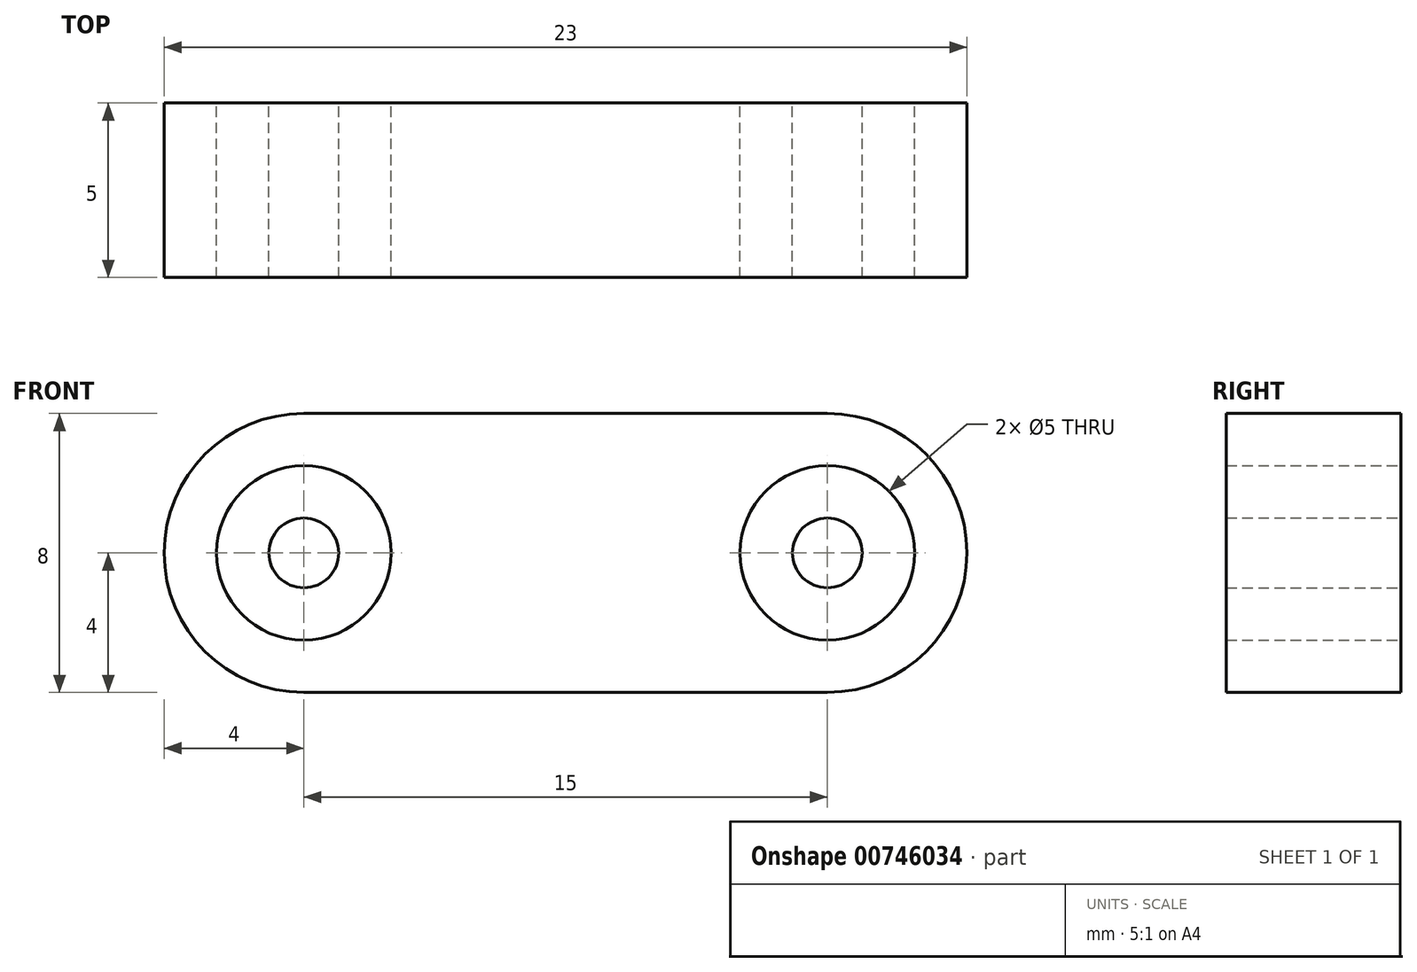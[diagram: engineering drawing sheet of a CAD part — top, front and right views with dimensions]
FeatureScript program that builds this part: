
annotation { "Feature Type Name" : "Feature", "Feature Type Description" : "" }
export const myFeature = defineFeature(function(context is Context, id is Id, definition is map)
    precondition{}
    {
        {
            var Q0;
            Q0=qCreatedBy(makeId("Front.planeOp"),FACE);
            var sketch = newSketch(context, id + "F0", { "sketchPlane" : qUnion([Q0])});
            skCircle(sketch, "E0", {"center": v(0, 0) * mm, "radius": 1 * mm});
            skCircle(sketch, "E1", {"center": v(0, 0) * mm, "radius": 2.5 * mm});
            skArc(sketch, "E2", {"start": v(0, 4) * mm, "mid": v(-4, 0) * mm, "end": v(0, -4) * mm});
            skArc(sketch, "E3", {"start": v(15, -4) * mm, "mid": v(19, 0) * mm, "end": v(15, 4) * mm});
            skCircle(sketch, "E4", {"center": v(15, 0) * mm, "radius": 2.5 * mm});
            skCircle(sketch, "E5", {"center": v(15, 0) * mm, "radius": 1 * mm});
            skLineSegment(sketch, "E6", {"start": v(0, 4) * mm, "end": v(15, 4) * mm});
            skLineSegment(sketch, "E7", {"start": v(0, -4) * mm, "end": v(15, -4) * mm});
            skSolve(sketch);
        }
        {
            var Q0;
            Q0=makeQuery(id+"F0.imprint","IMPRINT",FACE,{"disambiguationData":[TD([[makeQuery(id+"F0.imprint","IMPRINT",EDGE,{"derivedFrom":sQuery(id+"F0.wireOp",EDGE,"E1")}),-1.0]])]});
            var Q1;
            Q1=makeQuery(id+"F0.imprint","IMPRINT",FACE,{"disambiguationData":[TD([[makeQuery(id+"F0.imprint","IMPRINT",EDGE,{"derivedFrom":sQuery(id+"F0.wireOp",EDGE,"E0")}),1.0]])]});
            var Q2;
            Q2=makeQuery(id+"F0.imprint","IMPRINT",FACE,{"disambiguationData":[TD([[makeQuery(id+"F0.imprint","IMPRINT",EDGE,{"derivedFrom":sQuery(id+"F0.wireOp",EDGE,"E5")}),1.0]])]});
            extrude(context, id + "F1", {"entities" : qUnion([Q0, Q1, Q2]), "depth" : 5 * mm, "offsetDistance" : 25 * mm});
        }
    });
